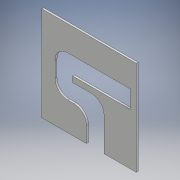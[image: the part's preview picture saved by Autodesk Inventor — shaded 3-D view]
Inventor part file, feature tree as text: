
AUTODESK INVENTOR PART (.ipt)
format: ipt  version: 2017 (Build 210142000, 142)  size: 123,904 bytes
history: native  units: mm
features: extrude x1, fillet x1, sketch x1
ambient origin geometry x8: Origin, YZ Plane, XZ Plane, XY Plane, X Axis, Y Axis, Z Axis, Center Point
bodies: Body1 (feature_tree)
feature tree (3):
  extrude  "Extrusion2"  Depth=300.0mm
  fillet  "Congé1"  Radius=300.0mm
  sketch  "Esquisse1"
